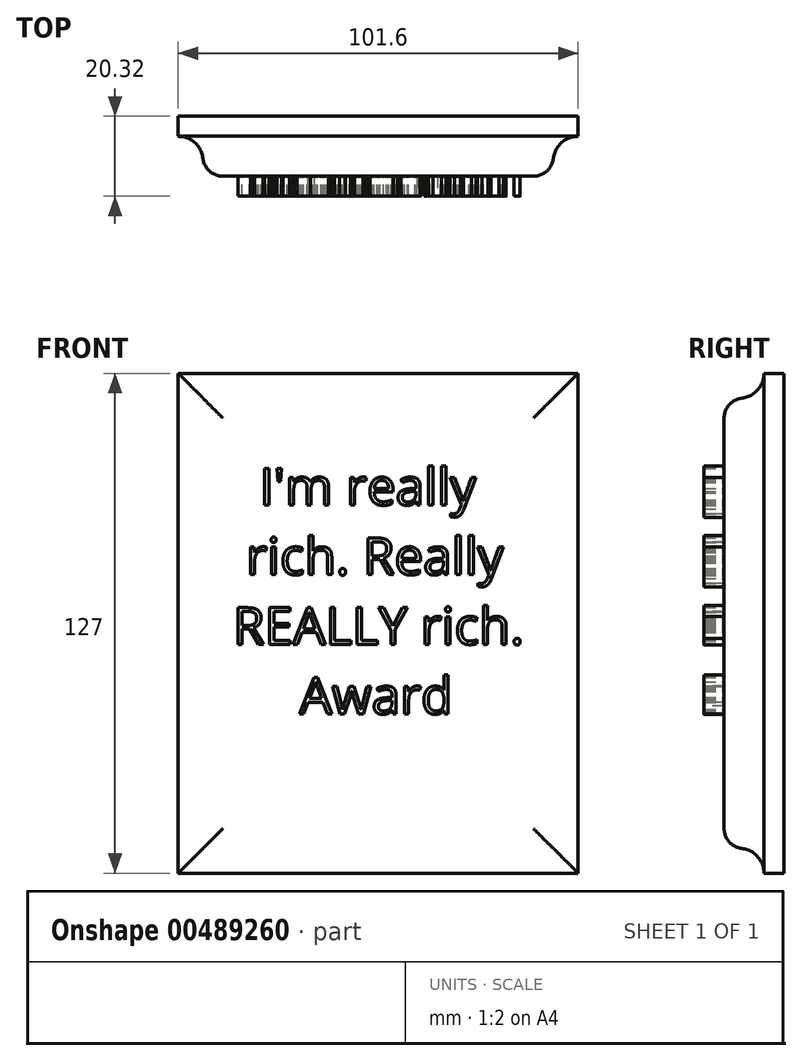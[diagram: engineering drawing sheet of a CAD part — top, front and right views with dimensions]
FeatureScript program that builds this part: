
annotation { "Feature Type Name" : "Feature", "Feature Type Description" : "" }
export const myFeature = defineFeature(function(context is Context, id is Id, definition is map)
    precondition{}
    {
        {
            var Q0;
            Q0=qCreatedBy(makeId("Front.planeOp"),FACE);
            var sketch = newSketch(context, id + "F0", { "sketchPlane" : qUnion([Q0])});
            skLineSegment(sketch, "E0.bottom", {"start": v(-101.6, 127) * mm, "end": v(0, 127) * mm});
            skLineSegment(sketch, "E0.top", {"start": v(-101.6, 0) * mm, "end": v(0, 0) * mm});
            skLineSegment(sketch, "E0.left", {"start": v(-101.6, 127) * mm, "end": v(-101.6, 0) * mm});
            skLineSegment(sketch, "E0.right", {"start": v(0, 127) * mm, "end": v(0, 0) * mm});
            skSolve(sketch);
        }
        {
            var Q0;
            Q0=qSketchRegion(id+"F0",true);
            extrude(context, id + "F1", {"entities" : qUnion([Q0]), "depth" : 15.24 * mm});
        }
        {
            var Q0;
            Q0=makeQuery(id+"F1.opExtrude","CAP_FACE",FACE,{"disambiguationData":[OSD([sQuery(id+"F0.wireOp",EDGE,"E0.bottom"),sQuery(id+"F0.wireOp",EDGE,"E0.top"),sQuery(id+"F0.wireOp",EDGE,"E0.left"),sQuery(id+"F0.wireOp",EDGE,"E0.right")])],"isStart":false});
            var sketch = newSketch(context, id + "F2", { "sketchPlane" : qUnion([Q0])});
            skLineSegment(sketch, "E1.bottom", {"start": v(-6.35, 6.35) * mm, "end": v(-95.25, 6.35) * mm});
            skLineSegment(sketch, "E1.top", {"start": v(-6.35, 120.65) * mm, "end": v(-95.25, 120.65) * mm});
            skLineSegment(sketch, "E1.left", {"start": v(-6.35, 6.35) * mm, "end": v(-6.35, 120.65) * mm});
            skLineSegment(sketch, "E1.right", {"start": v(-95.25, 6.35) * mm, "end": v(-95.25, 120.65) * mm});
            skLineSegment(sketch, "E2.bottom", {"start": v(-101.6, 127) * mm, "end": v(0, 127) * mm});
            skLineSegment(sketch, "E2.top", {"start": v(-101.6, 0) * mm, "end": v(0, 0) * mm});
            skLineSegment(sketch, "E2.left", {"start": v(-101.6, 127) * mm, "end": v(-101.6, 0) * mm});
            skLineSegment(sketch, "E2.right", {"start": v(0, 127) * mm, "end": v(0, 0) * mm});
            skSolve(sketch);
        }
        {
            var Q0;
            Q0=qSketchRegion(id+"F2",true);
            extrude(context, id + "F3", {"entities" : qUnion([Q0]), "operationType" : NewBodyOperationType.REMOVE, "oppositeDirection" : true, "depth" : 10.16 * mm});
        }
        {
            var Q0;
            Q0=makeQuery(id+"F3.boolean.opBoolean","COPY",EDGE,{"derivedFrom":makeQuery(id+"F3.opExtrude","CAP_EDGE",EDGE,{"disambiguationData":[OSD([sQuery(id+"F2.wireOp",EDGE,"E1.top")])],"isStart":false})});
            var Q1;
            Q1=makeQuery(id+"F3.boolean.opBoolean","COPY",EDGE,{"derivedFrom":makeQuery(id+"F3.opExtrude","CAP_EDGE",EDGE,{"disambiguationData":[OSD([sQuery(id+"F2.wireOp",EDGE,"E1.left")])],"isStart":false})});
            var Q2;
            Q2=makeQuery(id+"F3.boolean.opBoolean","COPY",EDGE,{"derivedFrom":makeQuery(id+"F3.opExtrude","CAP_EDGE",EDGE,{"disambiguationData":[OSD([sQuery(id+"F2.wireOp",EDGE,"E1.right")])],"isStart":false})});
            var Q3;
            Q3=makeQuery(id+"F3.boolean.opBoolean","COPY",EDGE,{"derivedFrom":makeQuery(id+"F3.opExtrude","CAP_EDGE",EDGE,{"disambiguationData":[OSD([sQuery(id+"F2.wireOp",EDGE,"E1.bottom")])],"isStart":false})});
            fillet(context, id + "F4", {"entities" : qUnion([Q0, Q1, Q2, Q3]), "radius" : 6.35 * mm, "tangentPropagation" : true, "allowEdgeOverflow" : false});
        }
        {
            var Q0;
            Q0=makeQuery(id+"F1.opExtrude","CAP_FACE",FACE,{"disambiguationData":[OSD([sQuery(id+"F0.wireOp",EDGE,"E0.bottom"),sQuery(id+"F0.wireOp",EDGE,"E0.top"),sQuery(id+"F0.wireOp",EDGE,"E0.left"),sQuery(id+"F0.wireOp",EDGE,"E0.right")])],"isStart":false});
            fillet(context, id + "F5", {"entities" : qUnion([Q0]), "radius" : 5.08 * mm, "tangentPropagation" : true, "allowEdgeOverflow" : false});
        }
        {
            var Q0;
            Q0=makeQuery(id+"F1.opExtrude","CAP_FACE",FACE,{"disambiguationData":[OSD([sQuery(id+"F0.wireOp",EDGE,"E0.bottom"),sQuery(id+"F0.wireOp",EDGE,"E0.top"),sQuery(id+"F0.wireOp",EDGE,"E0.left"),sQuery(id+"F0.wireOp",EDGE,"E0.right")])],"isStart":false});
            var sketch = newSketch(context, id + "F6", { "sketchPlane" : qUnion([Q0])});
            skText(sketch, "E3", { "text": "  I\'m really\n rich. Really\nREALLY rich.\n     Award", "fontName": "OpenSans-Regular.ttf"});
            const initialGuessF6  = {"E3": [-0.0877, 0.09357, 1, 0, 0.00937]};
            skSetInitialGuess(sketch, initialGuessF6);
            skSolve(sketch);
        }
        {
            var Q0;
            Q0=qSketchRegion(id+"F6",true);
            extrude(context, id + "F7", {"entities" : qUnion([Q0]), "operationType" : NewBodyOperationType.ADD, "depth" : 5.08 * mm});
        }
    });
